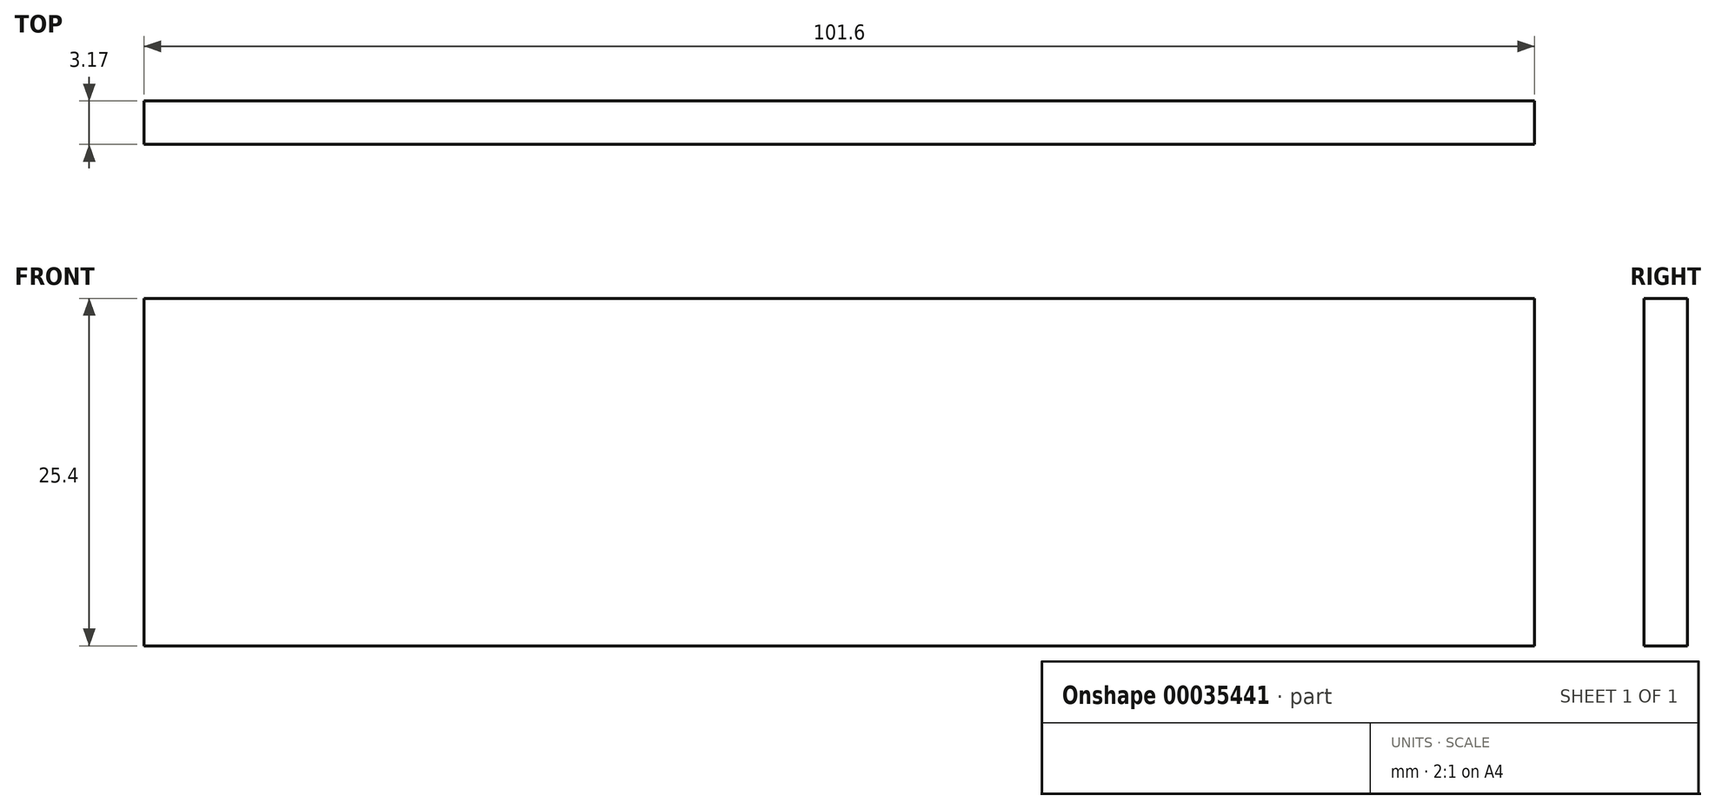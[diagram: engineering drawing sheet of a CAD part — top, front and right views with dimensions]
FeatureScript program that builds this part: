
annotation { "Feature Type Name" : "Feature", "Feature Type Description" : "" }
export const myFeature = defineFeature(function(context is Context, id is Id, definition is map)
    precondition{}
    {
        {
            var Q0;
            Q0=qCreatedBy(makeId("Front.planeOp"),FACE);
            var sketch = newSketch(context, id + "F0", { "sketchPlane" : qUnion([Q0])});
            skLineSegment(sketch, "E0.bottom", {"start": v(45.5, 25.4) * mm, "end": v(-56.1, 25.4) * mm});
            skLineSegment(sketch, "E0.top", {"start": v(45.5, 0) * mm, "end": v(-56.1, 0) * mm});
            skLineSegment(sketch, "E0.left", {"start": v(45.5, 25.4) * mm, "end": v(45.5, 0) * mm});
            skLineSegment(sketch, "E0.right", {"start": v(-56.1, 25.4) * mm, "end": v(-56.1, 0) * mm});
            skSolve(sketch);
        }
        {
            var Q0;
            Q0=makeQuery(id+"F0.imprint","IMPRINT",FACE,{"disambiguationData":[TD([[makeQuery(id+"F0.imprint","IMPRINT",EDGE,{"derivedFrom":sQuery(id+"F0.wireOp",EDGE,"E0.bottom")}),1.0]])]});
            extrude(context, id + "F1", {"entities" : qUnion([Q0]), "depth" : 3.17 * mm});
        }
    });
